# Revit family: IS_Eurovit_V9732_BIM_NL
name_source: partatom
category: Plumbing Fixtures
revit_build: Autodesk Revit MEP 2014 (Build: 20130308_1515(x64)
units: mm (PartAtom-declared; Revit-internal decimal feet)

## types (1)
- V973201 - EUROVIT PLANCHET 50CM WIT
    Accessories = www.idealstandardnederland.nl
    AreaUnits = millimeters
    Assembly Code = C1030200
    AssetType = Vast
    BIMObjectName = ISI_IdealStandard_BathroomShelves_V973201
    BREEAM = No
    BarCode = 8595095990432
    Brand = Ideal Standard
    Color = Wit
    ConnectionType = Sanitair
    Cost = 0 $
    Default Elevation = 1219 mm
    Description = Eurovit legplank 500 mm van keramiek.
    DurationUnit = jaar
    ECA = No
    ExpectedLife = 25
    Features = Legplank 500 mm van keramiek.
    Finish = Wit
    HWFU = 0
    IfcExportAs = IfcFurnitureType
    InstallationInstructions = http://www.idealstandardnederland.nl
    LinearUnits = millimeters
    ManufacturerURL = www.idealstandardnederland.nl
    Model = V973201
    ModelNumber = V973201
    ModelReference = Eurovit legplank 500 mm van keramiek.
    NBSDescription = Shelves
    NBSReference = 45-35-72/354
    Name = BathroomShelves_V973201_IdealStandard
    NettWeight = 3 kg
    NominalDepth = 0 mm  [stored 0 ft]
    NominalHeight = 63 mm
    NominalLength = 136 mm
    NominalWidth = 514 mm
    ProductInformation = http://www.idealstandardnederland.nl
    Shape = Gesculptuurd
    Size = 514 x 136 x 63 mm
    Space = Internal
    SpareParts = www.idealstandardnederland.nl
    TMV3 = No
    URL = www.idealstandardnederland.nl
    Uniclass2015Code = Pr_40_30_78_06
    Uniclass2015Title = Bathroom shelves
    Uniclass2015Version = Products v1.1
    Version = 1
    VolumeUnits = liter
    WRAS = No
    WarrantyDescription = Fabrieksgarantie
    WarrantyDurationParts = 5
    WarrantyDurationUnit = jaar
    WaterEfficientProduct = No

note: [stored X ft] marks values corroborated as IEEE doubles in the binary element streams (Revit-internal decimal feet)

## geometry (parser evidence)
native form markers: Sweep x2
no freeform markers — native parametric forms only
